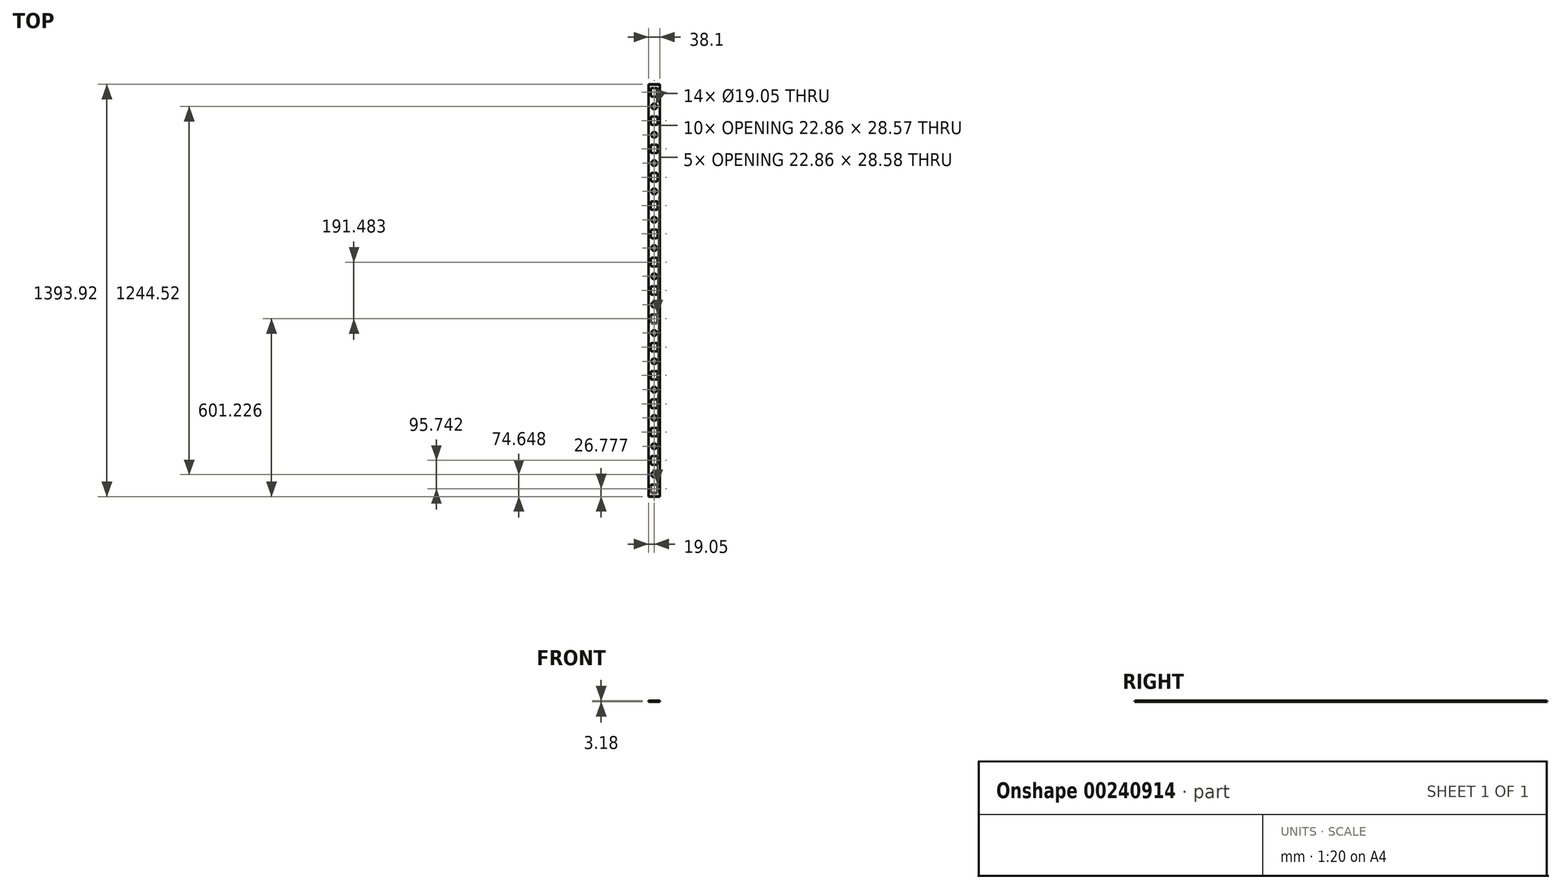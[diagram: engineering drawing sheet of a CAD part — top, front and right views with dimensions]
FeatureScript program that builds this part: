
annotation { "Feature Type Name" : "Feature", "Feature Type Description" : "" }
export const myFeature = defineFeature(function(context is Context, id is Id, definition is map)
    precondition{}
    {
        {
            var Q0;
            Q0=qCreatedBy(makeId("Front.planeOp"),FACE);
            var sketch = newSketch(context, id + "F0", { "sketchPlane" : qUnion([Q0])});
            skLineSegment(sketch, "E0.bottom", {"start": v(19.05, -1.59) * mm, "end": v(-19.05, -1.59) * mm});
            skLineSegment(sketch, "E0.top", {"start": v(19.05, 1.59) * mm, "end": v(-19.05, 1.59) * mm});
            skLineSegment(sketch, "E0.left", {"start": v(19.05, -1.59) * mm, "end": v(19.05, 1.59) * mm});
            skLineSegment(sketch, "E0.right", {"start": v(-19.05, -1.59) * mm, "end": v(-19.05, 1.59) * mm});
            skPoint(sketch, "E0.middle", {"position": v(0, 0) * mm});
            skSolve(sketch);
        }
        {
            var Q0;
            Q0=qSketchRegion(id+"F0",true);
            extrude(context, id + "F1", {"entities" : qUnion([Q0]), "depth" : 696.96 * mm, "hasSecondDirection" : true, "secondDirectionOppositeDirection" : true, "secondDirectionDepth" : 696.96 * mm});
        }
        {
            var Q0;
            Q0=makeQuery(id+"F1.opExtrude","SWEPT_FACE",FACE,{"disambiguationData":[OSD([sQuery(id+"F0.wireOp",EDGE,"E0.left")])]});
            var sketch = newSketch(context, id + "F2", { "sketchPlane" : qUnion([Q0])});
            skLineSegment(sketch, "E1", {"start": v(-696.96, -1.59) * mm, "end": v(-696.96, 1.59) * mm});
            skLineSegment(sketch, "E2", {"start": v(-696.96, -1.59) * mm, "end": v(-695.58, 1.59) * mm});
            skLineSegment(sketch, "E3", {"start": v(-695.58, 1.59) * mm, "end": v(-696.96, 1.59) * mm});
            skLineSegment(sketch, "E4", {"start": v(0, 0) * mm, "end": v(0, -127.2) * mm, "construction": true});
            skLineSegment(sketch, "E5.MirrorCS", {"start": v(696.96, -1.59) * mm, "end": v(695.58, 1.59) * mm});
            skLineSegment(sketch, "E6.MirrorCS", {"start": v(696.96, -1.59) * mm, "end": v(696.96, 1.59) * mm});
            skLineSegment(sketch, "E7.MirrorCS", {"start": v(695.58, 1.59) * mm, "end": v(696.96, 1.59) * mm});
            skSolve(sketch);
        }
        {
            var Q0;
            Q0=qSketchRegion(id+"F2",true);
            var Q1;
            Q1=makeQuery(id+"F1.opExtrude","SWEPT_FACE",FACE,{"disambiguationData":[OSD([sQuery(id+"F0.wireOp",EDGE,"E0.right")])]});
            extrude(context, id + "F3", {"entities" : qUnion([Q0]), "operationType" : NewBodyOperationType.REMOVE, "endBound" : BoundingType.UP_TO_SURFACE, "oppositeDirection" : true, "endBoundEntityFace" : qUnion([Q1]), "depth" : 25.4 * mm});
        }
        {
            var Q0;
            Q0=makeQuery(id+"F1.opExtrude","SWEPT_FACE",FACE,{"disambiguationData":[OSD([sQuery(id+"F0.wireOp",EDGE,"E0.top")])]});
            var sketch = newSketch(context, id + "F4", { "sketchPlane" : qUnion([Q0])});
            skLineSegment(sketch, "E8.bottom", {"start": v(7.62, -684.47) * mm, "end": v(-7.62, -684.47) * mm});
            skLineSegment(sketch, "E8.top", {"start": v(7.62, -655.9) * mm, "end": v(-7.62, -655.9) * mm});
            skLineSegment(sketch, "E8.left", {"start": v(11.43, -680.66) * mm, "end": v(11.43, -659.7) * mm});
            skLineSegment(sketch, "E8.right", {"start": v(-11.43, -680.66) * mm, "end": v(-11.43, -659.7) * mm});
            skPoint(sketch, "E8.middle", {"position": v(0, -670.18) * mm});
            skPoint(sketch, "E9.visualSharp", {"position": v(11.43, -655.9) * mm});
            skArc(sketch, "E9.filletArc", {"start": v(11.43, -659.7) * mm, "mid": v(10.31, -657.01) * mm, "end": v(7.62, -655.9) * mm});
            skPoint(sketch, "E10.visualSharp", {"position": v(-11.43, -655.9) * mm});
            skArc(sketch, "E10.filletArc", {"start": v(-7.62, -655.9) * mm, "mid": v(-10.31, -657.01) * mm, "end": v(-11.43, -659.7) * mm});
            skPoint(sketch, "E11.visualSharp", {"position": v(-11.43, -684.47) * mm});
            skArc(sketch, "E11.filletArc", {"start": v(-11.43, -680.66) * mm, "mid": v(-10.31, -683.35) * mm, "end": v(-7.62, -684.47) * mm});
            skPoint(sketch, "E12.visualSharp", {"position": v(11.43, -684.47) * mm});
            skArc(sketch, "E12.filletArc", {"start": v(7.62, -684.47) * mm, "mid": v(10.31, -683.35) * mm, "end": v(11.43, -680.66) * mm});
            skArc(sketch, "E13.0.1.0", {"start": v(7.62, -588.73) * mm, "mid": v(10.31, -587.61) * mm, "end": v(11.43, -584.92) * mm});
            skArc(sketch, "E13.0.1.1", {"start": v(11.43, -563.96) * mm, "mid": v(10.31, -561.27) * mm, "end": v(7.62, -560.15) * mm});
            skLineSegment(sketch, "E13.0.1.2", {"start": v(7.62, -560.15) * mm, "end": v(-7.62, -560.15) * mm});
            skLineSegment(sketch, "E13.0.1.3", {"start": v(-11.43, -584.92) * mm, "end": v(-11.43, -563.96) * mm});
            skArc(sketch, "E13.0.1.4", {"start": v(-11.43, -584.92) * mm, "mid": v(-10.31, -587.61) * mm, "end": v(-7.62, -588.73) * mm});
            skLineSegment(sketch, "E13.0.1.5", {"start": v(7.62, -588.73) * mm, "end": v(-7.62, -588.73) * mm});
            skLineSegment(sketch, "E13.0.1.6", {"start": v(11.43, -584.92) * mm, "end": v(11.43, -563.96) * mm});
            skArc(sketch, "E13.0.1.7", {"start": v(-7.62, -560.15) * mm, "mid": v(-10.31, -561.27) * mm, "end": v(-11.43, -563.96) * mm});
            skArc(sketch, "E13.0.2.0", {"start": v(7.62, -492.99) * mm, "mid": v(10.31, -491.87) * mm, "end": v(11.43, -489.18) * mm});
            skArc(sketch, "E13.0.2.1", {"start": v(11.43, -468.22) * mm, "mid": v(10.31, -465.53) * mm, "end": v(7.62, -464.41) * mm});
            skLineSegment(sketch, "E13.0.2.2", {"start": v(7.62, -464.41) * mm, "end": v(-7.62, -464.41) * mm});
            skLineSegment(sketch, "E13.0.2.3", {"start": v(-11.43, -489.18) * mm, "end": v(-11.43, -468.22) * mm});
            skArc(sketch, "E13.0.2.4", {"start": v(-11.43, -489.18) * mm, "mid": v(-10.31, -491.87) * mm, "end": v(-7.62, -492.99) * mm});
            skLineSegment(sketch, "E13.0.2.5", {"start": v(7.62, -492.99) * mm, "end": v(-7.62, -492.99) * mm});
            skLineSegment(sketch, "E13.0.2.6", {"start": v(11.43, -489.18) * mm, "end": v(11.43, -468.22) * mm});
            skArc(sketch, "E13.0.2.7", {"start": v(-7.62, -464.41) * mm, "mid": v(-10.31, -465.53) * mm, "end": v(-11.43, -468.22) * mm});
            skArc(sketch, "E13.0.3.0", {"start": v(7.62, -397.25) * mm, "mid": v(10.31, -396.13) * mm, "end": v(11.43, -393.44) * mm});
            skArc(sketch, "E13.0.3.1", {"start": v(11.43, -372.48) * mm, "mid": v(10.31, -369.79) * mm, "end": v(7.62, -368.67) * mm});
            skLineSegment(sketch, "E13.0.3.2", {"start": v(7.62, -368.67) * mm, "end": v(-7.62, -368.67) * mm});
            skLineSegment(sketch, "E13.0.3.3", {"start": v(-11.43, -393.44) * mm, "end": v(-11.43, -372.48) * mm});
            skArc(sketch, "E13.0.3.4", {"start": v(-11.43, -393.44) * mm, "mid": v(-10.31, -396.13) * mm, "end": v(-7.62, -397.25) * mm});
            skLineSegment(sketch, "E13.0.3.5", {"start": v(7.62, -397.25) * mm, "end": v(-7.62, -397.25) * mm});
            skLineSegment(sketch, "E13.0.3.6", {"start": v(11.43, -393.44) * mm, "end": v(11.43, -372.48) * mm});
            skArc(sketch, "E13.0.3.7", {"start": v(-7.62, -368.67) * mm, "mid": v(-10.31, -369.79) * mm, "end": v(-11.43, -372.48) * mm});
            skArc(sketch, "E13.0.4.0", {"start": v(7.62, -301.5) * mm, "mid": v(10.31, -300.39) * mm, "end": v(11.43, -297.7) * mm});
            skArc(sketch, "E13.0.4.1", {"start": v(11.43, -276.74) * mm, "mid": v(10.31, -274.05) * mm, "end": v(7.62, -272.93) * mm});
            skLineSegment(sketch, "E13.0.4.2", {"start": v(7.62, -272.93) * mm, "end": v(-7.62, -272.93) * mm});
            skLineSegment(sketch, "E13.0.4.3", {"start": v(-11.43, -297.7) * mm, "end": v(-11.43, -276.74) * mm});
            skArc(sketch, "E13.0.4.4", {"start": v(-11.43, -297.7) * mm, "mid": v(-10.31, -300.39) * mm, "end": v(-7.62, -301.5) * mm});
            skLineSegment(sketch, "E13.0.4.5", {"start": v(7.62, -301.5) * mm, "end": v(-7.62, -301.5) * mm});
            skLineSegment(sketch, "E13.0.4.6", {"start": v(11.43, -297.7) * mm, "end": v(11.43, -276.74) * mm});
            skArc(sketch, "E13.0.4.7", {"start": v(-7.62, -272.93) * mm, "mid": v(-10.31, -274.05) * mm, "end": v(-11.43, -276.74) * mm});
            skArc(sketch, "E13.0.5.0", {"start": v(7.62, -205.76) * mm, "mid": v(10.31, -204.65) * mm, "end": v(11.43, -201.95) * mm});
            skArc(sketch, "E13.0.5.1", {"start": v(11.43, -181) * mm, "mid": v(10.31, -178.3) * mm, "end": v(7.62, -177.19) * mm});
            skLineSegment(sketch, "E13.0.5.2", {"start": v(7.62, -177.19) * mm, "end": v(-7.62, -177.19) * mm});
            skLineSegment(sketch, "E13.0.5.3", {"start": v(-11.43, -201.95) * mm, "end": v(-11.43, -181) * mm});
            skArc(sketch, "E13.0.5.4", {"start": v(-11.43, -201.95) * mm, "mid": v(-10.31, -204.65) * mm, "end": v(-7.62, -205.76) * mm});
            skLineSegment(sketch, "E13.0.5.5", {"start": v(7.62, -205.76) * mm, "end": v(-7.62, -205.76) * mm});
            skLineSegment(sketch, "E13.0.5.6", {"start": v(11.43, -201.95) * mm, "end": v(11.43, -181) * mm});
            skArc(sketch, "E13.0.5.7", {"start": v(-7.62, -177.19) * mm, "mid": v(-10.31, -178.3) * mm, "end": v(-11.43, -181) * mm});
            skArc(sketch, "E13.0.6.0", {"start": v(7.62, -110.02) * mm, "mid": v(10.31, -108.9) * mm, "end": v(11.43, -106.21) * mm});
            skArc(sketch, "E13.0.6.1", {"start": v(11.43, -85.26) * mm, "mid": v(10.31, -82.56) * mm, "end": v(7.62, -81.45) * mm});
            skLineSegment(sketch, "E13.0.6.2", {"start": v(7.62, -81.45) * mm, "end": v(-7.62, -81.45) * mm});
            skLineSegment(sketch, "E13.0.6.3", {"start": v(-11.43, -106.21) * mm, "end": v(-11.43, -85.26) * mm});
            skArc(sketch, "E13.0.6.4", {"start": v(-11.43, -106.21) * mm, "mid": v(-10.31, -108.9) * mm, "end": v(-7.62, -110.02) * mm});
            skLineSegment(sketch, "E13.0.6.5", {"start": v(7.62, -110.02) * mm, "end": v(-7.62, -110.02) * mm});
            skLineSegment(sketch, "E13.0.6.6", {"start": v(11.43, -106.21) * mm, "end": v(11.43, -85.26) * mm});
            skArc(sketch, "E13.0.6.7", {"start": v(-7.62, -81.45) * mm, "mid": v(-10.31, -82.56) * mm, "end": v(-11.43, -85.26) * mm});
            skArc(sketch, "E13.0.7.0", {"start": v(7.62, -14.28) * mm, "mid": v(10.31, -13.16) * mm, "end": v(11.43, -10.47) * mm});
            skArc(sketch, "E13.0.7.1", {"start": v(11.43, 10.49) * mm, "mid": v(10.31, 13.18) * mm, "end": v(7.62, 14.3) * mm});
            skLineSegment(sketch, "E13.0.7.2", {"start": v(7.62, 14.3) * mm, "end": v(-7.62, 14.3) * mm});
            skLineSegment(sketch, "E13.0.7.3", {"start": v(-11.43, -10.47) * mm, "end": v(-11.43, 10.49) * mm});
            skArc(sketch, "E13.0.7.4", {"start": v(-11.43, -10.47) * mm, "mid": v(-10.31, -13.16) * mm, "end": v(-7.62, -14.28) * mm});
            skLineSegment(sketch, "E13.0.7.5", {"start": v(7.62, -14.28) * mm, "end": v(-7.62, -14.28) * mm});
            skLineSegment(sketch, "E13.0.7.6", {"start": v(11.43, -10.47) * mm, "end": v(11.43, 10.49) * mm});
            skArc(sketch, "E13.0.7.7", {"start": v(-7.62, 14.3) * mm, "mid": v(-10.31, 13.18) * mm, "end": v(-11.43, 10.49) * mm});
            skArc(sketch, "E13.0.8.0", {"start": v(7.62, 81.46) * mm, "mid": v(10.31, 82.58) * mm, "end": v(11.43, 85.27) * mm});
            skArc(sketch, "E13.0.8.1", {"start": v(11.43, 106.23) * mm, "mid": v(10.31, 108.92) * mm, "end": v(7.62, 110.04) * mm});
            skLineSegment(sketch, "E13.0.8.2", {"start": v(7.62, 110.04) * mm, "end": v(-7.62, 110.04) * mm});
            skLineSegment(sketch, "E13.0.8.3", {"start": v(-11.43, 85.27) * mm, "end": v(-11.43, 106.23) * mm});
            skArc(sketch, "E13.0.8.4", {"start": v(-11.43, 85.27) * mm, "mid": v(-10.31, 82.58) * mm, "end": v(-7.62, 81.46) * mm});
            skLineSegment(sketch, "E13.0.8.5", {"start": v(7.62, 81.46) * mm, "end": v(-7.62, 81.46) * mm});
            skLineSegment(sketch, "E13.0.8.6", {"start": v(11.43, 85.27) * mm, "end": v(11.43, 106.23) * mm});
            skArc(sketch, "E13.0.8.7", {"start": v(-7.62, 110.04) * mm, "mid": v(-10.31, 108.92) * mm, "end": v(-11.43, 106.23) * mm});
            skArc(sketch, "E13.0.9.0", {"start": v(7.62, 177.2) * mm, "mid": v(10.31, 178.32) * mm, "end": v(11.43, 181.01) * mm});
            skArc(sketch, "E13.0.9.1", {"start": v(11.43, 201.97) * mm, "mid": v(10.31, 204.66) * mm, "end": v(7.62, 205.78) * mm});
            skLineSegment(sketch, "E13.0.9.2", {"start": v(7.62, 205.78) * mm, "end": v(-7.62, 205.78) * mm});
            skLineSegment(sketch, "E13.0.9.3", {"start": v(-11.43, 181.01) * mm, "end": v(-11.43, 201.97) * mm});
            skArc(sketch, "E13.0.9.4", {"start": v(-11.43, 181.01) * mm, "mid": v(-10.31, 178.32) * mm, "end": v(-7.62, 177.2) * mm});
            skLineSegment(sketch, "E13.0.9.5", {"start": v(7.62, 177.2) * mm, "end": v(-7.62, 177.2) * mm});
            skLineSegment(sketch, "E13.0.9.6", {"start": v(11.43, 181.01) * mm, "end": v(11.43, 201.97) * mm});
            skArc(sketch, "E13.0.9.7", {"start": v(-7.62, 205.78) * mm, "mid": v(-10.31, 204.66) * mm, "end": v(-11.43, 201.97) * mm});
            skArc(sketch, "E13.0.10.0", {"start": v(7.62, 272.94) * mm, "mid": v(10.31, 274.06) * mm, "end": v(11.43, 276.75) * mm});
            skArc(sketch, "E13.0.10.1", {"start": v(11.43, 297.7) * mm, "mid": v(10.31, 300.4) * mm, "end": v(7.62, 301.52) * mm});
            skLineSegment(sketch, "E13.0.10.2", {"start": v(7.62, 301.52) * mm, "end": v(-7.62, 301.52) * mm});
            skLineSegment(sketch, "E13.0.10.3", {"start": v(-11.43, 276.75) * mm, "end": v(-11.43, 297.7) * mm});
            skArc(sketch, "E13.0.10.4", {"start": v(-11.43, 276.75) * mm, "mid": v(-10.31, 274.06) * mm, "end": v(-7.62, 272.94) * mm});
            skLineSegment(sketch, "E13.0.10.5", {"start": v(7.62, 272.94) * mm, "end": v(-7.62, 272.94) * mm});
            skLineSegment(sketch, "E13.0.10.6", {"start": v(11.43, 276.75) * mm, "end": v(11.43, 297.7) * mm});
            skArc(sketch, "E13.0.10.7", {"start": v(-7.62, 301.52) * mm, "mid": v(-10.31, 300.4) * mm, "end": v(-11.43, 297.7) * mm});
            skArc(sketch, "E13.0.11.0", {"start": v(7.62, 368.69) * mm, "mid": v(10.31, 369.8) * mm, "end": v(11.43, 372.5) * mm});
            skArc(sketch, "E13.0.11.1", {"start": v(11.43, 393.45) * mm, "mid": v(10.31, 396.15) * mm, "end": v(7.62, 397.26) * mm});
            skLineSegment(sketch, "E13.0.11.2", {"start": v(7.62, 397.26) * mm, "end": v(-7.62, 397.26) * mm});
            skLineSegment(sketch, "E13.0.11.3", {"start": v(-11.43, 372.5) * mm, "end": v(-11.43, 393.45) * mm});
            skArc(sketch, "E13.0.11.4", {"start": v(-11.43, 372.5) * mm, "mid": v(-10.31, 369.8) * mm, "end": v(-7.62, 368.69) * mm});
            skLineSegment(sketch, "E13.0.11.5", {"start": v(7.62, 368.69) * mm, "end": v(-7.62, 368.69) * mm});
            skLineSegment(sketch, "E13.0.11.6", {"start": v(11.43, 372.5) * mm, "end": v(11.43, 393.45) * mm});
            skArc(sketch, "E13.0.11.7", {"start": v(-7.62, 397.26) * mm, "mid": v(-10.31, 396.15) * mm, "end": v(-11.43, 393.45) * mm});
            skArc(sketch, "E13.0.12.0", {"start": v(7.62, 464.43) * mm, "mid": v(10.31, 465.54) * mm, "end": v(11.43, 468.24) * mm});
            skArc(sketch, "E13.0.12.1", {"start": v(11.43, 489.2) * mm, "mid": v(10.31, 491.89) * mm, "end": v(7.62, 493) * mm});
            skLineSegment(sketch, "E13.0.12.2", {"start": v(7.62, 493) * mm, "end": v(-7.62, 493) * mm});
            skLineSegment(sketch, "E13.0.12.3", {"start": v(-11.43, 468.24) * mm, "end": v(-11.43, 489.2) * mm});
            skArc(sketch, "E13.0.12.4", {"start": v(-11.43, 468.24) * mm, "mid": v(-10.31, 465.54) * mm, "end": v(-7.62, 464.43) * mm});
            skLineSegment(sketch, "E13.0.12.5", {"start": v(7.62, 464.43) * mm, "end": v(-7.62, 464.43) * mm});
            skLineSegment(sketch, "E13.0.12.6", {"start": v(11.43, 468.24) * mm, "end": v(11.43, 489.2) * mm});
            skArc(sketch, "E13.0.12.7", {"start": v(-7.62, 493) * mm, "mid": v(-10.31, 491.89) * mm, "end": v(-11.43, 489.2) * mm});
            skArc(sketch, "E13.0.13.0", {"start": v(7.62, 560.17) * mm, "mid": v(10.31, 561.28) * mm, "end": v(11.43, 563.98) * mm});
            skArc(sketch, "E13.0.13.1", {"start": v(11.43, 584.93) * mm, "mid": v(10.31, 587.63) * mm, "end": v(7.62, 588.74) * mm});
            skLineSegment(sketch, "E13.0.13.2", {"start": v(7.62, 588.74) * mm, "end": v(-7.62, 588.74) * mm});
            skLineSegment(sketch, "E13.0.13.3", {"start": v(-11.43, 563.98) * mm, "end": v(-11.43, 584.93) * mm});
            skArc(sketch, "E13.0.13.4", {"start": v(-11.43, 563.98) * mm, "mid": v(-10.31, 561.28) * mm, "end": v(-7.62, 560.17) * mm});
            skLineSegment(sketch, "E13.0.13.5", {"start": v(7.62, 560.17) * mm, "end": v(-7.62, 560.17) * mm});
            skLineSegment(sketch, "E13.0.13.6", {"start": v(11.43, 563.98) * mm, "end": v(11.43, 584.93) * mm});
            skArc(sketch, "E13.0.13.7", {"start": v(-7.62, 588.74) * mm, "mid": v(-10.31, 587.63) * mm, "end": v(-11.43, 584.93) * mm});
            skArc(sketch, "E13.0.14.0", {"start": v(7.62, 655.91) * mm, "mid": v(10.31, 657.03) * mm, "end": v(11.43, 659.72) * mm});
            skArc(sketch, "E13.0.14.1", {"start": v(11.43, 680.68) * mm, "mid": v(10.31, 683.37) * mm, "end": v(7.62, 684.49) * mm});
            skLineSegment(sketch, "E13.0.14.2", {"start": v(7.62, 684.49) * mm, "end": v(-7.62, 684.49) * mm});
            skLineSegment(sketch, "E13.0.14.3", {"start": v(-11.43, 659.72) * mm, "end": v(-11.43, 680.68) * mm});
            skArc(sketch, "E13.0.14.4", {"start": v(-11.43, 659.72) * mm, "mid": v(-10.31, 657.03) * mm, "end": v(-7.62, 655.91) * mm});
            skLineSegment(sketch, "E13.0.14.5", {"start": v(7.62, 655.91) * mm, "end": v(-7.62, 655.91) * mm});
            skLineSegment(sketch, "E13.0.14.6", {"start": v(11.43, 659.72) * mm, "end": v(11.43, 680.68) * mm});
            skArc(sketch, "E13.0.14.7", {"start": v(-7.62, 684.49) * mm, "mid": v(-10.31, 683.37) * mm, "end": v(-11.43, 680.68) * mm});
            skLineSegment(sketch, "E13.direction1", {"start": v(11.43, -680.66) * mm, "end": v(36.83, -680.66) * mm, "construction": true});
            skLineSegment(sketch, "E13.direction2", {"start": v(11.43, -680.66) * mm, "end": v(11.43, -584.92) * mm, "construction": true});
            skLineSegment(sketch, "E14", {"start": v(-11.43, -584.92) * mm, "end": v(-11.43, -659.7) * mm, "construction": true});
            skLineSegment(sketch, "E15", {"start": v(-11.43, -622.31) * mm, "end": v(11.43, -622.31) * mm, "construction": true});
            skCircle(sketch, "E16", {"center": v(0, -622.31) * mm, "radius": 9.53 * mm});
            skCircle(sketch, "E17.0.1.0", {"center": v(0, -526.58) * mm, "radius": 9.53 * mm});
            skCircle(sketch, "E17.0.2.0", {"center": v(0, -430.85) * mm, "radius": 9.53 * mm});
            skCircle(sketch, "E17.0.3.0", {"center": v(0, -335.11) * mm, "radius": 9.53 * mm});
            skCircle(sketch, "E17.0.4.0", {"center": v(0, -239.38) * mm, "radius": 9.53 * mm});
            skCircle(sketch, "E17.0.5.0", {"center": v(0, -143.65) * mm, "radius": 9.53 * mm});
            skCircle(sketch, "E17.0.6.0", {"center": v(0, -47.92) * mm, "radius": 9.53 * mm});
            skCircle(sketch, "E17.0.7.0", {"center": v(0, 47.82) * mm, "radius": 9.53 * mm});
            skCircle(sketch, "E17.0.8.0", {"center": v(0, 143.55) * mm, "radius": 9.53 * mm});
            skCircle(sketch, "E17.0.9.0", {"center": v(0, 239.28) * mm, "radius": 9.53 * mm});
            skCircle(sketch, "E17.0.10.0", {"center": v(0, 335.01) * mm, "radius": 9.53 * mm});
            skCircle(sketch, "E17.0.11.0", {"center": v(0, 430.75) * mm, "radius": 9.53 * mm});
            skCircle(sketch, "E17.0.12.0", {"center": v(0, 526.48) * mm, "radius": 9.53 * mm});
            skCircle(sketch, "E17.0.13.0", {"center": v(0, 622.21) * mm, "radius": 9.53 * mm});
            skLineSegment(sketch, "E17.direction1", {"start": v(0, -622.31) * mm, "end": v(25.4, -622.31) * mm, "construction": true});
            skLineSegment(sketch, "E17.direction2", {"start": v(0, -622.31) * mm, "end": v(0, -526.58) * mm, "construction": true});
            skSolve(sketch);
        }
        {
            var Q0;
            Q0=qSketchRegion(id+"F4",true);
            var Q1;
            Q1=makeQuery(id+"F1.opExtrude","SWEPT_FACE",FACE,{"disambiguationData":[OSD([sQuery(id+"F0.wireOp",EDGE,"E0.bottom")])]});
            extrude(context, id + "F5", {"entities" : qUnion([Q0]), "operationType" : NewBodyOperationType.REMOVE, "endBound" : BoundingType.UP_TO_SURFACE, "oppositeDirection" : true, "endBoundEntityFace" : qUnion([Q1]), "depth" : 25.4 * mm});
        }
    });
